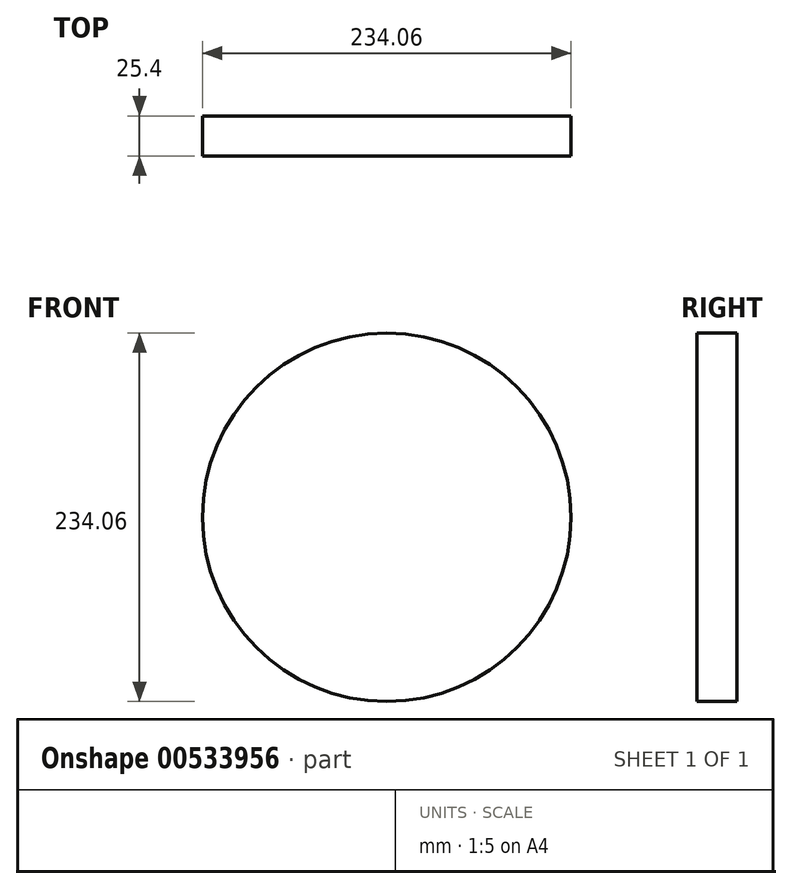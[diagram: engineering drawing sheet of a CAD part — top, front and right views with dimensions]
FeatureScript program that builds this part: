
annotation { "Feature Type Name" : "Feature", "Feature Type Description" : "" }
export const myFeature = defineFeature(function(context is Context, id is Id, definition is map)
    precondition{}
    {
        {
            var Q0;
            Q0=qCreatedBy(makeId("Front.planeOp"),FACE);
            var sketch = newSketch(context, id + "F0", { "sketchPlane" : qUnion([Q0])});
            skCircle(sketch, "E0", {"center": v(-31, 33) * mm, "radius": 117.03 * mm});
            skSolve(sketch);
        }
        {
            var Q0;
            Q0 = qSketchRegion(id + "F0", true);
            extrude(context, id + "F1", {"entities" : qUnion([Q0]), "depth" : 25.4 * mm, "offsetDistance" : 25.4 * mm});
        }
    });
